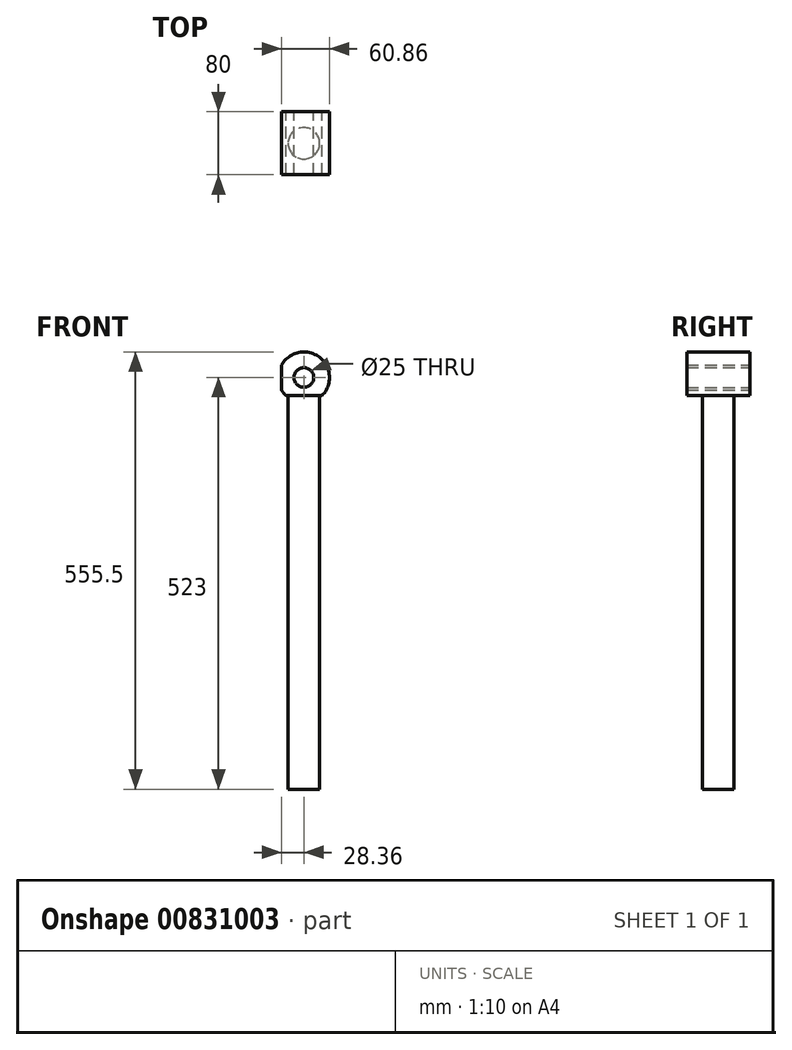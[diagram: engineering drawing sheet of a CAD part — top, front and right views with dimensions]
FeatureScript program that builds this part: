
annotation { "Feature Type Name" : "Feature", "Feature Type Description" : "" }
export const myFeature = defineFeature(function(context is Context, id is Id, definition is map)
    precondition{}
    {
        {
            var Q0;
            Q0=qCreatedBy(makeId("Front.planeOp"),FACE);
            var sketch = newSketch(context, id + "F0", { "sketchPlane" : qUnion([Q0])});
            skCircle(sketch, "E0", {"center": v(0, 0) * mm, "radius": 12.5 * mm});
            skArc(sketch, "E1", {"start": v(22.96, -23) * mm, "mid": v(0, 32.5) * mm, "end": v(-22.96, -23) * mm});
            skLineSegment(sketch, "E2", {"start": v(-46.89, -23) * mm, "end": v(63.7, -23) * mm});
            skLineSegment(sketch, "E3", {"start": v(-28.36, -23) * mm, "end": v(-28.36, 32.48) * mm});
            skSolve(sketch);
        }
        {
            var Q0;
            Q0=makeQuery(id+"F0.imprint","IMPRINT",FACE,{"disambiguationData":[TD([[makeQuery(id+"F0.imprint","IMPRINT",EDGE,{"derivedFrom":sQuery(id+"F0.wireOp",EDGE,"E0")}),-1.0]])]});
            extrude(context, id + "F1", {"entities" : qUnion([Q0]), "endBound" : BoundingType.SYMMETRIC, "depth" : 80 * mm, "offsetDistance" : 25 * mm});
        }
        {
            var Q0;
            Q0=makeQuery(id+"F1.opExtrude","SWEPT_FACE",FACE,{"disambiguationData":[OSD([sQuery(id+"F0.wireOp",EDGE,"E2")])]});
            var sketch = newSketch(context, id + "F2", { "sketchPlane" : qUnion([Q0])});
            skCircle(sketch, "E4", {"center": v(0, 0) * mm, "radius": 20 * mm});
            skSolve(sketch);
        }
        {
            var Q0;
            Q0=makeQuery(id+"F2.imprint","IMPRINT",FACE,{"disambiguationData":[TD([[makeQuery(id+"F2.imprint","IMPRINT",EDGE,{"derivedFrom":sQuery(id+"F2.wireOp",EDGE,"E4")}),1.0]])]});
            extrude(context, id + "F3", {"entities" : qUnion([Q0]), "operationType" : NewBodyOperationType.ADD, "depth" : 500 * mm, "offsetDistance" : 25 * mm});
        }
    });
